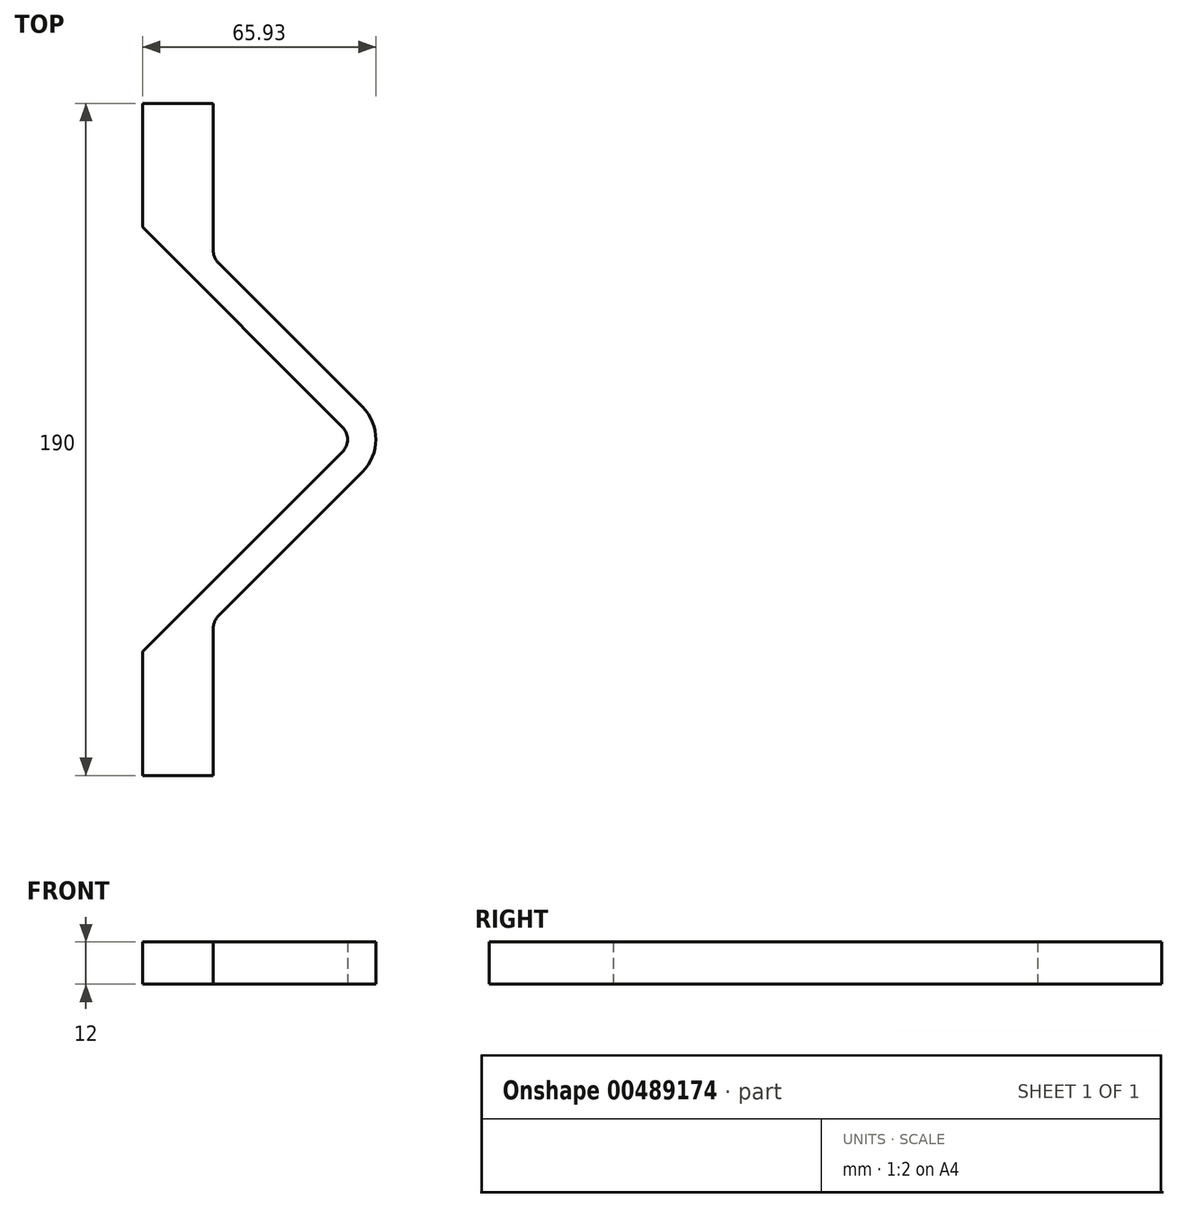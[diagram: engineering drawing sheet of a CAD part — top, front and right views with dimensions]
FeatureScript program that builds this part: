
annotation { "Feature Type Name" : "Feature", "Feature Type Description" : "" }
export const myFeature = defineFeature(function(context is Context, id is Id, definition is map)
    precondition{}
    {
        {
            var Q0;
            Q0=qCreatedBy(makeId("Top.planeOp"),FACE);
            var sketch = newSketch(context, id + "F0", { "sketchPlane" : qUnion([Q0])});
            skLineSegment(sketch, "E0", {"start": v(-9.2, 9.2) * mm, "end": v(-49.85, 49.85) * mm});
            skLineSegment(sketch, "E1", {"start": v(-51.31, 53.38) * mm, "end": v(-51.31, 95) * mm});
            skLineSegment(sketch, "E2", {"start": v(-51.31, 95) * mm, "end": v(-71.31, 95) * mm});
            skLineSegment(sketch, "E3", {"start": v(-71.31, 95) * mm, "end": v(-71.31, 60) * mm});
            skLineSegment(sketch, "E4", {"start": v(-71.31, 60) * mm, "end": v(-14.85, 3.54) * mm});
            skLineSegment(sketch, "E5.MirrorCS", {"start": v(-71.31, -60) * mm, "end": v(-14.85, -3.54) * mm});
            skLineSegment(sketch, "E6.MirrorCS", {"start": v(-71.31, -95) * mm, "end": v(-71.31, -60) * mm});
            skLineSegment(sketch, "E7.MirrorCS", {"start": v(-51.31, -53.38) * mm, "end": v(-51.31, -95) * mm});
            skLineSegment(sketch, "E8.MirrorCS", {"start": v(-51.31, -95) * mm, "end": v(-71.31, -95) * mm});
            skLineSegment(sketch, "E9.MirrorCS", {"start": v(-9.2, -9.2) * mm, "end": v(-49.85, -49.85) * mm});
            skPoint(sketch, "E10.visualSharp", {"position": v(-11.31, 0) * mm});
            skArc(sketch, "E10.filletArc", {"start": v(-14.85, -3.54) * mm, "mid": v(-13.38, 0) * mm, "end": v(-14.85, 3.54) * mm});
            skPoint(sketch, "E11.visualSharp", {"position": v(0, 0) * mm});
            skArc(sketch, "E11.filletArc", {"start": v(-9.2, -9.2) * mm, "mid": v(-5.38, 0) * mm, "end": v(-9.2, 9.2) * mm});
            skPoint(sketch, "E12.visualSharp", {"position": v(-51.31, 51.31) * mm});
            skArc(sketch, "E12.filletArc", {"start": v(-51.31, 53.38) * mm, "mid": v(-50.93, 51.47) * mm, "end": v(-49.85, 49.85) * mm});
            skPoint(sketch, "E13.visualSharp", {"position": v(-51.31, -51.31) * mm});
            skArc(sketch, "E13.filletArc", {"start": v(-49.85, -49.85) * mm, "mid": v(-50.93, -51.47) * mm, "end": v(-51.31, -53.38) * mm});
            skSolve(sketch);
        }
        {
            var Q0;
            Q0=makeQuery(id+"F0.imprint","IMPRINT",FACE,{"disambiguationData":[TD([[makeQuery(id+"F0.imprint","IMPRINT",EDGE,{"derivedFrom":sQuery(id+"F0.wireOp",EDGE,"E0")}),1.0]])]});
            extrude(context, id + "F1", {"entities" : qUnion([Q0]), "depth" : 12 * mm});
        }
    });
